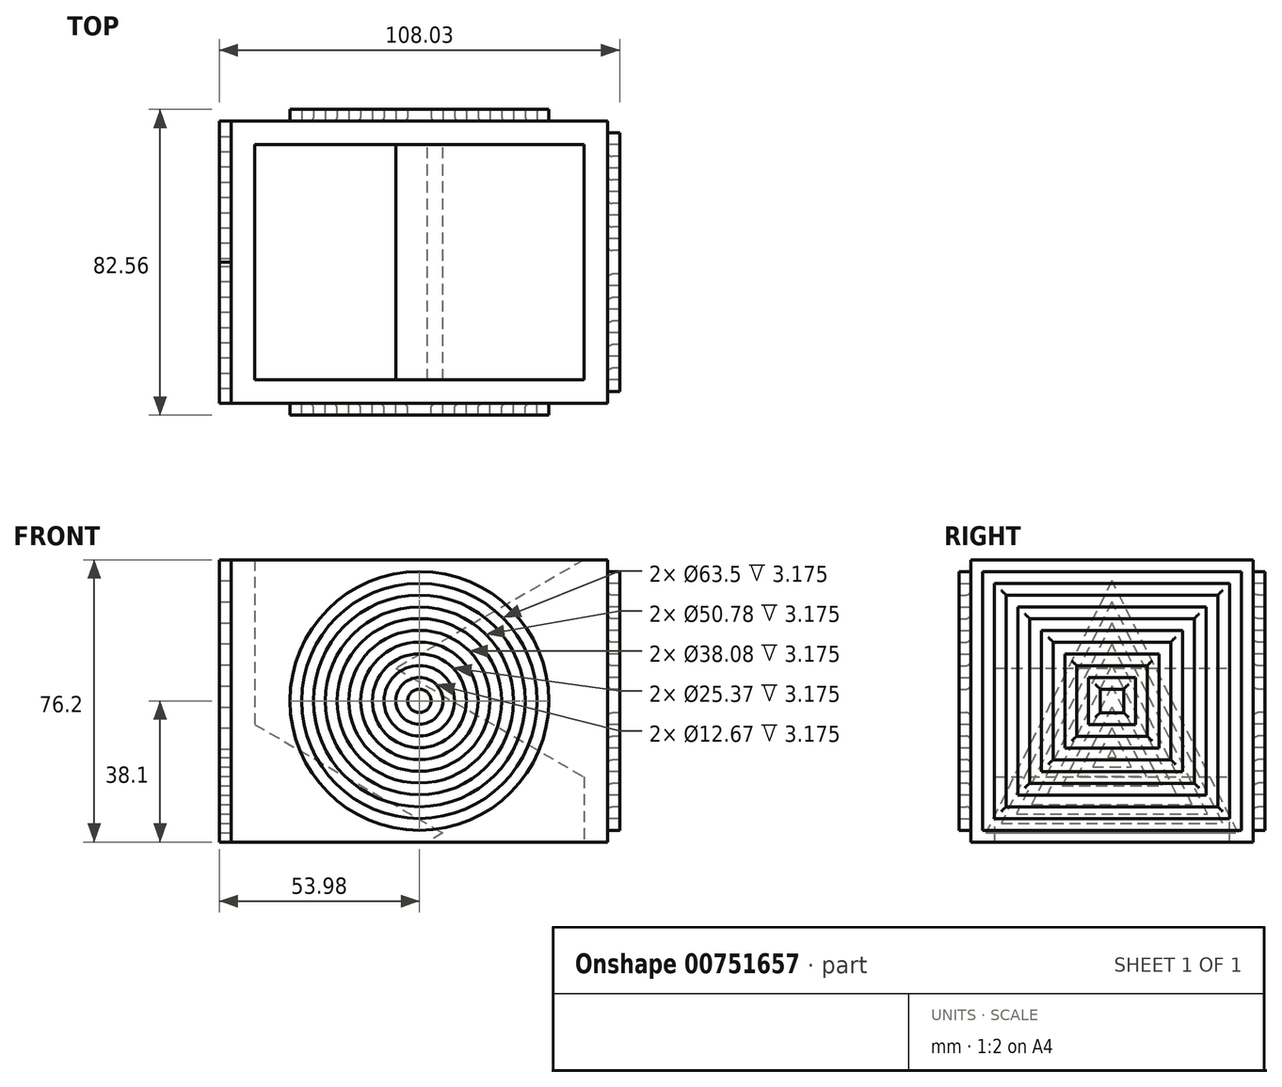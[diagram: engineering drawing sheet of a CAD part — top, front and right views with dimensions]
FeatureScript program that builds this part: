
annotation { "Feature Type Name" : "Feature", "Feature Type Description" : "" }
export const myFeature = defineFeature(function(context is Context, id is Id, definition is map)
    precondition{}
    {
        {
            var Q0;
            Q0=qCreatedBy(makeId("Front.planeOp"),FACE);
            var sketch = newSketch(context, id + "F0", { "sketchPlane" : qUnion([Q0])});
            skLineSegment(sketch, "E0", {"start": v(50.8, 38.1) * mm, "end": v(50.8, -38.1) * mm});
            skLineSegment(sketch, "E1", {"start": v(50.8, 38.1) * mm, "end": v(-50.8, 38.1) * mm});
            skLineSegment(sketch, "E2.MirrorCS", {"start": v(-50.8, 38.1) * mm, "end": v(-50.8, -38.1) * mm});
            skLineSegment(sketch, "E3.MirrorCS", {"start": v(-50.8, 38.1) * mm, "end": v(50.8, 38.1) * mm});
            skLineSegment(sketch, "E4.MirrorCS", {"start": v(-50.8, -38.1) * mm, "end": v(50.8, -38.1) * mm});
            skLineSegment(sketch, "E5", {"start": v(44.45, 38.1) * mm, "end": v(44.45, -38.1) * mm});
            skLineSegment(sketch, "E6", {"start": v(-44.45, 38.1) * mm, "end": v(-44.45, -38.1) * mm});
            skLineSegment(sketch, "E7", {"start": v(44.45, 38.1) * mm, "end": v(-6.35, 8.77) * mm});
            skLineSegment(sketch, "E8", {"start": v(-6.35, 8.77) * mm, "end": v(44.45, -20.56) * mm});
            skLineSegment(sketch, "E9", {"start": v(-44.45, -6.35) * mm, "end": v(6.35, -35.68) * mm});
            skLineSegment(sketch, "E10", {"start": v(6.35, -35.68) * mm, "end": v(2.16, -38.1) * mm});
            skSolve(sketch);
        }
        {
            var Q0;
            {var subQ0=sQuery(id+"F0.wireOp",EDGE,"E7");Q0=makeQuery(id+"F0.imprint","IMPRINT",FACE,{"disambiguationData":[TD([[makeQuery(id+"F0.imprint","IMPRINT",EDGE,{"derivedFrom":subQ0}),1.0]])]});}
            var Q1;
            {var subQ1=sQuery(id+"F0.wireOp",EDGE,"E0");Q1=makeQuery(id+"F0.imprint","IMPRINT",FACE,{"disambiguationData":[TD([[makeQuery(id+"F0.imprint","IMPRINT",EDGE,{"derivedFrom":subQ1}),-1.0]])]});}
            var Q2;
            {var subQ4=sQuery(id+"F0.wireOp",EDGE,"E9");Q2=makeQuery(id+"F0.imprint","IMPRINT",FACE,{"disambiguationData":[TD([[makeQuery(id+"F0.imprint","IMPRINT",EDGE,{"derivedFrom":subQ4}),-1.0]])]});}
            var Q3;
            {var subQ1=sQuery(id+"F0.wireOp",EDGE,"E2.MirrorCS");Q3=makeQuery(id+"F0.imprint","IMPRINT",FACE,{"disambiguationData":[TD([[makeQuery(id+"F0.imprint","IMPRINT",EDGE,{"derivedFrom":subQ1}),1.0]])]});}
            extrude(context, id + "F1", {"entities" : qUnion([Q0, Q1, Q2, Q3]), "endBound" : BoundingType.SYMMETRIC, "depth" : 76.2 * mm, "offsetDistance" : 25.4 * mm});
        }
        {
            var Q0;
            Q0=makeQuery(id+"F1.opExtrude","CAP_FACE",FACE,{"disambiguationData":[OSD([sQuery(id+"F0.wireOp",EDGE,"E0"),sQuery(id+"F0.wireOp",EDGE,"E3.MirrorCS"),sQuery(id+"F0.wireOp",EDGE,"E4.MirrorCS"),sQuery(id+"F0.wireOp",EDGE,"E5"),sQuery(id+"F0.wireOp",EDGE,"E7"),sQuery(id+"F0.wireOp",EDGE,"E8")])],"isStart":true});
            var sketch = newSketch(context, id + "F2", { "sketchPlane" : qUnion([Q0])});
            skLineSegment(sketch, "E11.bottom", {"start": v(50.8, 38.1) * mm, "end": v(-50.8, 38.1) * mm});
            skLineSegment(sketch, "E11.top", {"start": v(50.8, -38.1) * mm, "end": v(-50.8, -38.1) * mm});
            skLineSegment(sketch, "E11.left", {"start": v(50.8, 38.1) * mm, "end": v(50.8, -38.1) * mm});
            skLineSegment(sketch, "E11.right", {"start": v(-50.8, 38.1) * mm, "end": v(-50.8, -38.1) * mm});
            skPoint(sketch, "E11.middle", {"position": v(0, 0) * mm});
            skSolve(sketch);
        }
        {
            var Q0;
            Q0 = qSketchRegion(id + "F2", true);
            extrude(context, id + "F3", {"entities" : qUnion([Q0]), "operationType" : NewBodyOperationType.ADD, "oppositeDirection" : true, "depth" : 6.35 * mm, "offsetDistance" : 25.4 * mm});
        }
        {
            var Q0;
            Q0=makeQuery(id+"F1.opExtrude","CAP_FACE",FACE,{"disambiguationData":[OSD([sQuery(id+"F0.wireOp",EDGE,"E0"),sQuery(id+"F0.wireOp",EDGE,"E3.MirrorCS"),sQuery(id+"F0.wireOp",EDGE,"E4.MirrorCS"),sQuery(id+"F0.wireOp",EDGE,"E5"),sQuery(id+"F0.wireOp",EDGE,"E7"),sQuery(id+"F0.wireOp",EDGE,"E8")])],"isStart":false});
            var sketch = newSketch(context, id + "F4", { "sketchPlane" : qUnion([Q0])});
            skLineSegment(sketch, "E12.bottom", {"start": v(50.8, -38.1) * mm, "end": v(-50.8, -38.1) * mm});
            skLineSegment(sketch, "E12.top", {"start": v(50.8, 38.1) * mm, "end": v(-50.8, 38.1) * mm});
            skLineSegment(sketch, "E12.left", {"start": v(50.8, -38.1) * mm, "end": v(50.8, 38.1) * mm});
            skLineSegment(sketch, "E12.right", {"start": v(-50.8, -38.1) * mm, "end": v(-50.8, 38.1) * mm});
            skPoint(sketch, "E12.middle", {"position": v(0, 0) * mm});
            skSolve(sketch);
        }
        {
            var Q0;
            Q0 = qSketchRegion(id + "F4", true);
            extrude(context, id + "F5", {"entities" : qUnion([Q0]), "operationType" : NewBodyOperationType.ADD, "oppositeDirection" : true, "depth" : 6.35 * mm, "offsetDistance" : 25.4 * mm});
        }
        {
            var Q0;
            Q0=makeQuery(id+"F1.opExtrude","SWEPT_FACE",FACE,{"disambiguationData":[OSD([sQuery(id+"F0.wireOp",EDGE,"E0")])]});
            var sketch = newSketch(context, id + "F6", { "sketchPlane" : qUnion([Q0])});
            skLineSegment(sketch, "E13.bottom", {"start": v(-34.93, 34.92) * mm, "end": v(34.93, 34.92) * mm});
            skLineSegment(sketch, "E13.top", {"start": v(-34.93, -34.92) * mm, "end": v(34.93, -34.92) * mm});
            skLineSegment(sketch, "E13.left", {"start": v(-34.92, 34.92) * mm, "end": v(-34.92, -34.92) * mm});
            skLineSegment(sketch, "E13.right", {"start": v(34.93, 34.92) * mm, "end": v(34.93, -34.92) * mm});
            skPoint(sketch, "E13.middle", {"position": v(0, 0) * mm});
            skLineSegment(sketch, "E14.bottom", {"start": v(-31.75, 31.75) * mm, "end": v(31.75, 31.75) * mm});
            skLineSegment(sketch, "E14.top", {"start": v(-31.75, -31.75) * mm, "end": v(31.75, -31.75) * mm});
            skLineSegment(sketch, "E14.left", {"start": v(-31.75, 31.75) * mm, "end": v(-31.75, -31.75) * mm});
            skLineSegment(sketch, "E14.right", {"start": v(31.75, 31.75) * mm, "end": v(31.75, -31.75) * mm});
            skLineSegment(sketch, "E15.bottom", {"start": v(-28.57, 28.57) * mm, "end": v(28.57, 28.57) * mm});
            skLineSegment(sketch, "E15.top", {"start": v(-28.57, -28.57) * mm, "end": v(28.57, -28.57) * mm});
            skLineSegment(sketch, "E15.left", {"start": v(-28.57, 28.57) * mm, "end": v(-28.57, -28.57) * mm});
            skLineSegment(sketch, "E15.right", {"start": v(28.58, 28.57) * mm, "end": v(28.58, -28.57) * mm});
            skLineSegment(sketch, "E16.bottom", {"start": v(-25.4, 25.4) * mm, "end": v(25.4, 25.4) * mm});
            skLineSegment(sketch, "E16.top", {"start": v(-25.4, -25.4) * mm, "end": v(25.4, -25.4) * mm});
            skLineSegment(sketch, "E16.left", {"start": v(-25.4, 25.4) * mm, "end": v(-25.4, -25.4) * mm});
            skLineSegment(sketch, "E16.right", {"start": v(25.4, 25.4) * mm, "end": v(25.4, -25.4) * mm});
            skLineSegment(sketch, "E17.bottom", {"start": v(-22.23, 22.23) * mm, "end": v(22.23, 22.23) * mm});
            skLineSegment(sketch, "E17.top", {"start": v(-22.23, -22.23) * mm, "end": v(22.23, -22.23) * mm});
            skLineSegment(sketch, "E17.left", {"start": v(-22.23, 22.23) * mm, "end": v(-22.23, -22.23) * mm});
            skLineSegment(sketch, "E17.right", {"start": v(22.23, 22.23) * mm, "end": v(22.23, -22.23) * mm});
            skLineSegment(sketch, "E18.bottom", {"start": v(-19.05, 19.05) * mm, "end": v(19.05, 19.05) * mm});
            skLineSegment(sketch, "E18.top", {"start": v(-19.05, -19.05) * mm, "end": v(19.05, -19.05) * mm});
            skLineSegment(sketch, "E18.left", {"start": v(-19.05, 19.05) * mm, "end": v(-19.05, -19.05) * mm});
            skLineSegment(sketch, "E18.right", {"start": v(19.05, 19.05) * mm, "end": v(19.05, -19.05) * mm});
            skLineSegment(sketch, "E19.bottom", {"start": v(-15.88, 15.88) * mm, "end": v(15.88, 15.88) * mm});
            skLineSegment(sketch, "E19.top", {"start": v(-15.88, -15.88) * mm, "end": v(15.88, -15.88) * mm});
            skLineSegment(sketch, "E19.left", {"start": v(-15.88, 15.88) * mm, "end": v(-15.88, -15.88) * mm});
            skLineSegment(sketch, "E19.right", {"start": v(15.88, 15.88) * mm, "end": v(15.88, -15.88) * mm});
            skLineSegment(sketch, "E20.bottom", {"start": v(-12.7, 12.7) * mm, "end": v(12.7, 12.7) * mm});
            skLineSegment(sketch, "E20.top", {"start": v(-12.7, -12.7) * mm, "end": v(12.7, -12.7) * mm});
            skLineSegment(sketch, "E20.left", {"start": v(-12.7, 12.7) * mm, "end": v(-12.7, -12.7) * mm});
            skLineSegment(sketch, "E20.right", {"start": v(12.7, 12.7) * mm, "end": v(12.7, -12.7) * mm});
            skLineSegment(sketch, "E21.bottom", {"start": v(-9.52, 9.52) * mm, "end": v(9.52, 9.52) * mm});
            skLineSegment(sketch, "E21.top", {"start": v(-9.52, -9.52) * mm, "end": v(9.52, -9.52) * mm});
            skLineSegment(sketch, "E21.left", {"start": v(-9.52, 9.52) * mm, "end": v(-9.52, -9.52) * mm});
            skLineSegment(sketch, "E21.right", {"start": v(9.52, 9.52) * mm, "end": v(9.52, -9.52) * mm});
            skLineSegment(sketch, "E22.bottom", {"start": v(-6.35, 6.35) * mm, "end": v(6.35, 6.35) * mm});
            skLineSegment(sketch, "E22.top", {"start": v(-6.35, -6.35) * mm, "end": v(6.35, -6.35) * mm});
            skLineSegment(sketch, "E22.left", {"start": v(-6.35, 6.35) * mm, "end": v(-6.35, -6.35) * mm});
            skLineSegment(sketch, "E22.right", {"start": v(6.35, 6.35) * mm, "end": v(6.35, -6.35) * mm});
            skLineSegment(sketch, "E23.bottom", {"start": v(-3.17, 3.17) * mm, "end": v(3.17, 3.17) * mm});
            skLineSegment(sketch, "E23.top", {"start": v(-3.17, -3.17) * mm, "end": v(3.17, -3.17) * mm});
            skLineSegment(sketch, "E23.left", {"start": v(-3.17, 3.17) * mm, "end": v(-3.17, -3.17) * mm});
            skLineSegment(sketch, "E23.right", {"start": v(3.17, 3.17) * mm, "end": v(3.17, -3.17) * mm});
            skSolve(sketch);
        }
        {
            var Q0;
            Q0 = qSketchRegion(id + "F6", true);
            var Q1;
            Q1=makeQuery(id+"F6.imprint","IMPRINT",FACE,{"disambiguationData":[TD([[makeQuery(id+"F6.imprint","IMPRINT",EDGE,{"derivedFrom":sQuery(id+"F6.wireOp",EDGE,"E15.bottom")}),-1.0]])]});
            var Q2;
            Q2=makeQuery(id+"F6.imprint","IMPRINT",FACE,{"disambiguationData":[TD([[makeQuery(id+"F6.imprint","IMPRINT",EDGE,{"derivedFrom":sQuery(id+"F6.wireOp",EDGE,"E17.bottom")}),-1.0]])]});
            var Q3;
            Q3=makeQuery(id+"F6.imprint","IMPRINT",FACE,{"disambiguationData":[TD([[makeQuery(id+"F6.imprint","IMPRINT",EDGE,{"derivedFrom":sQuery(id+"F6.wireOp",EDGE,"E19.bottom")}),-1.0]])]});
            var Q4;
            Q4=makeQuery(id+"F6.imprint","IMPRINT",FACE,{"disambiguationData":[TD([[makeQuery(id+"F6.imprint","IMPRINT",EDGE,{"derivedFrom":sQuery(id+"F6.wireOp",EDGE,"E21.bottom")}),-1.0]])]});
            var Q5;
            Q5=makeQuery(id+"F6.imprint","IMPRINT",FACE,{"disambiguationData":[TD([[makeQuery(id+"F6.imprint","IMPRINT",EDGE,{"derivedFrom":sQuery(id+"F6.wireOp",EDGE,"E23.bottom")}),-1.0]])]});
            extrude(context, id + "F7", {"entities" : qUnion([Q0, Q1, Q2, Q3, Q4, Q5]), "operationType" : NewBodyOperationType.ADD, "depth" : 3.25 * mm, "offsetDistance" : 25.4 * mm});
        }
        {
            var Q0;
            {var subQ0=sQuery(id+"F0.wireOp",EDGE,"E4.MirrorCS");var subQ1=sQuery(id+"F0.wireOp",EDGE,"E3.MirrorCS");Q0=makeQuery(id+"F3.boolean.opBoolean","MERGE",FACE,{"derivedFrom":[makeQuery(id+"F1.opExtrude","CAP_FACE",FACE,{"disambiguationData":[OSD([sQuery(id+"F0.wireOp",EDGE,"E0"),subQ1,subQ0,sQuery(id+"F0.wireOp",EDGE,"E5"),sQuery(id+"F0.wireOp",EDGE,"E7"),sQuery(id+"F0.wireOp",EDGE,"E8")])],"isStart":true}),makeQuery(id+"F1.opExtrude","CAP_FACE",FACE,{"disambiguationData":[OSD([sQuery(id+"F0.wireOp",EDGE,"E2.MirrorCS"),subQ1,subQ0,sQuery(id+"F0.wireOp",EDGE,"E6"),sQuery(id+"F0.wireOp",EDGE,"E9"),sQuery(id+"F0.wireOp",EDGE,"E10")])],"isStart":true}),makeQuery(id+"F3.opExtrude","CAP_FACE",FACE,{"disambiguationData":[OSD([sQuery(id+"F2.wireOp",EDGE,"E11.bottom"),sQuery(id+"F2.wireOp",EDGE,"E11.top"),sQuery(id+"F2.wireOp",EDGE,"E11.left"),sQuery(id+"F2.wireOp",EDGE,"E11.right")])],"isStart":true})]});}
            var sketch = newSketch(context, id + "F8", { "sketchPlane" : qUnion([Q0])});
            skCircle(sketch, "E24", {"center": v(0, 0) * mm, "radius": 34.93 * mm});
            skCircle(sketch, "E25", {"center": v(0, 0) * mm, "radius": 31.75 * mm});
            skCircle(sketch, "E26", {"center": v(0, 0) * mm, "radius": 28.58 * mm});
            skCircle(sketch, "E27", {"center": v(0, 0) * mm, "radius": 25.4 * mm});
            skCircle(sketch, "E28", {"center": v(0, 0) * mm, "radius": 22.22 * mm});
            skCircle(sketch, "E29", {"center": v(0, 0) * mm, "radius": 19.04 * mm});
            skCircle(sketch, "E30", {"center": v(0, 0) * mm, "radius": 15.86 * mm});
            skCircle(sketch, "E31", {"center": v(0, 0) * mm, "radius": 12.68 * mm});
            skCircle(sketch, "E32", {"center": v(0, 0) * mm, "radius": 9.5 * mm});
            skCircle(sketch, "E33", {"center": v(0, 0) * mm, "radius": 6.33 * mm});
            skCircle(sketch, "E34", {"center": v(0, 0) * mm, "radius": 3.16 * mm});
            skSolve(sketch);
        }
        {
            var Q0;
            Q0 = qSketchRegion(id + "F8", true);
            var Q1;
            Q1=makeQuery(id+"F8.imprint","IMPRINT",FACE,{"disambiguationData":[TD([[makeQuery(id+"F8.imprint","IMPRINT",EDGE,{"derivedFrom":sQuery(id+"F8.wireOp",EDGE,"E26")}),1.0]])]});
            var Q2;
            Q2=makeQuery(id+"F8.imprint","IMPRINT",FACE,{"disambiguationData":[TD([[makeQuery(id+"F8.imprint","IMPRINT",EDGE,{"derivedFrom":sQuery(id+"F8.wireOp",EDGE,"E28")}),1.0]])]});
            var Q3;
            Q3=makeQuery(id+"F8.imprint","IMPRINT",FACE,{"disambiguationData":[TD([[makeQuery(id+"F8.imprint","IMPRINT",EDGE,{"derivedFrom":sQuery(id+"F8.wireOp",EDGE,"E30")}),1.0]])]});
            var Q4;
            Q4=makeQuery(id+"F8.imprint","IMPRINT",FACE,{"disambiguationData":[TD([[makeQuery(id+"F8.imprint","IMPRINT",EDGE,{"derivedFrom":sQuery(id+"F8.wireOp",EDGE,"E32")}),1.0]])]});
            var Q5;
            Q5=makeQuery(id+"F8.imprint","IMPRINT",FACE,{"disambiguationData":[TD([[makeQuery(id+"F8.imprint","IMPRINT",EDGE,{"derivedFrom":sQuery(id+"F8.wireOp",EDGE,"E34")}),1.0]])]});
            extrude(context, id + "F9", {"entities" : qUnion([Q0, Q1, Q2, Q3, Q4, Q5]), "operationType" : NewBodyOperationType.ADD, "depth" : 3.17 * mm, "offsetDistance" : 25.4 * mm});
        }
        {
            var Q0;
            Q0=makeQuery(id+"F7.opExtrude","CAP_EDGE",EDGE,{"disambiguationData":[OSD([sQuery(id+"F6.wireOp",EDGE,"E13.left")])],"isStart":true});
            var Q1;
            Q1=makeQuery(id+"F7.opExtrude","CAP_EDGE",EDGE,{"disambiguationData":[OSD([sQuery(id+"F6.wireOp",EDGE,"E13.bottom")])],"isStart":true});
            var Q2;
            Q2=makeQuery(id+"F7.opExtrude","CAP_EDGE",EDGE,{"disambiguationData":[OSD([sQuery(id+"F6.wireOp",EDGE,"E13.right")])],"isStart":true});
            var Q3;
            Q3=makeQuery(id+"F7.opExtrude","CAP_EDGE",EDGE,{"disambiguationData":[OSD([sQuery(id+"F6.wireOp",EDGE,"E13.top")])],"isStart":true});
            var Q4;
            Q4=makeQuery(id+"F7.opExtrude","CAP_EDGE",EDGE,{"disambiguationData":[OSD([sQuery(id+"F6.wireOp",EDGE,"E15.right")])],"isStart":true});
            var Q5;
            Q5=makeQuery(id+"F7.opExtrude","CAP_EDGE",EDGE,{"disambiguationData":[OSD([sQuery(id+"F6.wireOp",EDGE,"E15.bottom")])],"isStart":true});
            var Q6;
            Q6=makeQuery(id+"F7.opExtrude","CAP_EDGE",EDGE,{"disambiguationData":[OSD([sQuery(id+"F6.wireOp",EDGE,"E15.left")])],"isStart":true});
            var Q7;
            Q7=makeQuery(id+"F7.opExtrude","CAP_EDGE",EDGE,{"disambiguationData":[OSD([sQuery(id+"F6.wireOp",EDGE,"E15.top")])],"isStart":true});
            var Q8;
            Q8=makeQuery(id+"F7.opExtrude","CAP_EDGE",EDGE,{"disambiguationData":[OSD([sQuery(id+"F6.wireOp",EDGE,"E17.top")])],"isStart":true});
            var Q9;
            Q9=makeQuery(id+"F7.opExtrude","CAP_EDGE",EDGE,{"disambiguationData":[OSD([sQuery(id+"F6.wireOp",EDGE,"E17.left")])],"isStart":true});
            var Q10;
            Q10=makeQuery(id+"F7.opExtrude","CAP_EDGE",EDGE,{"disambiguationData":[OSD([sQuery(id+"F6.wireOp",EDGE,"E17.right")])],"isStart":true});
            var Q11;
            Q11=makeQuery(id+"F7.opExtrude","CAP_EDGE",EDGE,{"disambiguationData":[OSD([sQuery(id+"F6.wireOp",EDGE,"E17.bottom")])],"isStart":true});
            var Q12;
            Q12=makeQuery(id+"F7.opExtrude","CAP_EDGE",EDGE,{"disambiguationData":[OSD([sQuery(id+"F6.wireOp",EDGE,"E19.bottom")])],"isStart":true});
            var Q13;
            Q13=makeQuery(id+"F7.opExtrude","CAP_EDGE",EDGE,{"disambiguationData":[OSD([sQuery(id+"F6.wireOp",EDGE,"E19.right")])],"isStart":true});
            var Q14;
            Q14=makeQuery(id+"F7.opExtrude","CAP_EDGE",EDGE,{"disambiguationData":[OSD([sQuery(id+"F6.wireOp",EDGE,"E21.bottom")])],"isStart":true});
            var Q15;
            Q15=makeQuery(id+"F7.opExtrude","CAP_EDGE",EDGE,{"disambiguationData":[OSD([sQuery(id+"F6.wireOp",EDGE,"E21.right")])],"isStart":true});
            var Q16;
            Q16=makeQuery(id+"F7.opExtrude","CAP_EDGE",EDGE,{"disambiguationData":[OSD([sQuery(id+"F6.wireOp",EDGE,"E23.bottom")])],"isStart":true});
            var Q17;
            Q17=makeQuery(id+"F7.opExtrude","CAP_EDGE",EDGE,{"disambiguationData":[OSD([sQuery(id+"F6.wireOp",EDGE,"E23.right")])],"isStart":true});
            var Q18;
            Q18=makeQuery(id+"F7.opExtrude","CAP_EDGE",EDGE,{"disambiguationData":[OSD([sQuery(id+"F6.wireOp",EDGE,"E23.left")])],"isStart":true});
            var Q19;
            Q19=makeQuery(id+"F7.opExtrude","CAP_EDGE",EDGE,{"disambiguationData":[OSD([sQuery(id+"F6.wireOp",EDGE,"E23.top")])],"isStart":true});
            var Q20;
            Q20=makeQuery(id+"F7.opExtrude","CAP_EDGE",EDGE,{"disambiguationData":[OSD([sQuery(id+"F6.wireOp",EDGE,"E21.left")])],"isStart":true});
            var Q21;
            Q21=makeQuery(id+"F7.opExtrude","CAP_EDGE",EDGE,{"disambiguationData":[OSD([sQuery(id+"F6.wireOp",EDGE,"E21.top")])],"isStart":true});
            var Q22;
            Q22=makeQuery(id+"F7.opExtrude","CAP_EDGE",EDGE,{"disambiguationData":[OSD([sQuery(id+"F6.wireOp",EDGE,"E19.left")])],"isStart":true});
            var Q23;
            Q23=makeQuery(id+"F7.opExtrude","CAP_EDGE",EDGE,{"disambiguationData":[OSD([sQuery(id+"F6.wireOp",EDGE,"E19.top")])],"isStart":true});
            fillet(context, id + "F10", {"entities" : qUnion([Q0, Q1, Q2, Q3, Q4, Q5, Q6, Q7, Q8, Q9, Q10, Q11, Q12, Q13, Q14, Q15, Q16, Q17, Q18, Q19, Q20, Q21, Q22, Q23]), "radius" : 1.27 * mm, "tangentPropagation" : true, "allowEdgeOverflow" : false});
        }
        {
            var Q0;
            Q0=makeQuery(id+"F9.opExtrude","CAP_EDGE",EDGE,{"disambiguationData":[OSD([sQuery(id+"F8.wireOp",EDGE,"E24")])],"isStart":true});
            var Q1;
            Q1=makeQuery(id+"F9.opExtrude","CAP_EDGE",EDGE,{"disambiguationData":[OSD([sQuery(id+"F8.wireOp",EDGE,"E26")])],"isStart":true});
            var Q2;
            Q2=makeQuery(id+"F9.opExtrude","CAP_EDGE",EDGE,{"disambiguationData":[OSD([sQuery(id+"F8.wireOp",EDGE,"E28")])],"isStart":true});
            var Q3;
            Q3=makeQuery(id+"F9.opExtrude","CAP_EDGE",EDGE,{"disambiguationData":[OSD([sQuery(id+"F8.wireOp",EDGE,"E30")])],"isStart":true});
            var Q4;
            Q4=makeQuery(id+"F9.opExtrude","CAP_EDGE",EDGE,{"disambiguationData":[OSD([sQuery(id+"F8.wireOp",EDGE,"E32")])],"isStart":true});
            var Q5;
            Q5=makeQuery(id+"F9.opExtrude","CAP_EDGE",EDGE,{"disambiguationData":[OSD([sQuery(id+"F8.wireOp",EDGE,"E34")])],"isStart":true});
            fillet(context, id + "F11", {"entities" : qUnion([Q0, Q1, Q2, Q3, Q4, Q5]), "radius" : 1.27 * mm, "tangentPropagation" : true, "allowEdgeOverflow" : false});
        }
        {
            var Q0;
            Q0=makeQuery(id+"F1.opExtrude","SWEPT_BODY",BODY,{"disambiguationData":[OSD([sQuery(id+"F0.wireOp",EDGE,"E0"),sQuery(id+"F0.wireOp",EDGE,"E3.MirrorCS"),sQuery(id+"F0.wireOp",EDGE,"E4.MirrorCS"),sQuery(id+"F0.wireOp",EDGE,"E5"),sQuery(id+"F0.wireOp",EDGE,"E7"),sQuery(id+"F0.wireOp",EDGE,"E8")])]});
            var Q1;
            Q1=qCreatedBy(makeId("Front.planeOp"),FACE);
            mirror(context, id + "F12", {"operationType" : NewBodyOperationType.ADD, "entities" : qUnion([Q0]), "mirrorPlane" : qUnion([Q1])});
        }
        {
            var Q0;
            Q0=makeQuery(id+"F1.opExtrude","SWEPT_FACE",FACE,{"disambiguationData":[OSD([sQuery(id+"F0.wireOp",EDGE,"E2.MirrorCS")])]});
            var sketch = newSketch(context, id + "F13", { "sketchPlane" : qUnion([Q0])});
            skLineSegment(sketch, "E35.0", {"start": v(38.1, -38.1) * mm, "end": v(-38.1, -38.1) * mm});
            skLineSegment(sketch, "E36", {"start": v(-38.1, -38.1) * mm, "end": v(0, 38.1) * mm});
            skLineSegment(sketch, "E37", {"start": v(0, 38.1) * mm, "end": v(38.1, -38.1) * mm});
            skLineSegment(sketch, "E38.0", {"start": v(-34, -35.56) * mm, "end": v(0, 32.42) * mm});
            skLineSegment(sketch, "E38.1", {"start": v(34, -35.56) * mm, "end": v(-34, -35.56) * mm});
            skLineSegment(sketch, "E38.2", {"start": v(0, 32.42) * mm, "end": v(34, -35.56) * mm});
            skLineSegment(sketch, "E39.0", {"start": v(-29.88, -33.02) * mm, "end": v(0, 26.74) * mm});
            skLineSegment(sketch, "E39.1", {"start": v(29.88, -33.02) * mm, "end": v(-29.88, -33.02) * mm});
            skLineSegment(sketch, "E39.2", {"start": v(0, 26.74) * mm, "end": v(29.88, -33.02) * mm});
            skLineSegment(sketch, "E40.0", {"start": v(-25.77, -30.48) * mm, "end": v(0, 21.06) * mm});
            skLineSegment(sketch, "E40.1", {"start": v(25.77, -30.48) * mm, "end": v(-25.77, -30.48) * mm});
            skLineSegment(sketch, "E40.2", {"start": v(0, 21.06) * mm, "end": v(25.77, -30.48) * mm});
            skLineSegment(sketch, "E41.0", {"start": v(-21.66, -27.94) * mm, "end": v(0, 15.38) * mm});
            skLineSegment(sketch, "E41.1", {"start": v(21.66, -27.94) * mm, "end": v(-21.66, -27.94) * mm});
            skLineSegment(sketch, "E41.2", {"start": v(0, 15.38) * mm, "end": v(21.66, -27.94) * mm});
            skLineSegment(sketch, "E42.0", {"start": v(-17.55, -25.4) * mm, "end": v(0, 9.7) * mm});
            skLineSegment(sketch, "E42.1", {"start": v(17.55, -25.4) * mm, "end": v(-17.55, -25.4) * mm});
            skLineSegment(sketch, "E42.2", {"start": v(0, 9.7) * mm, "end": v(17.55, -25.4) * mm});
            skLineSegment(sketch, "E43.0", {"start": v(-13.44, -22.86) * mm, "end": v(0, 4.02) * mm});
            skLineSegment(sketch, "E43.1", {"start": v(13.44, -22.86) * mm, "end": v(-13.44, -22.86) * mm});
            skLineSegment(sketch, "E43.2", {"start": v(0, 4.02) * mm, "end": v(13.44, -22.86) * mm});
            skLineSegment(sketch, "E44.0", {"start": v(-9.33, -20.32) * mm, "end": v(0, -1.66) * mm});
            skLineSegment(sketch, "E44.1", {"start": v(9.33, -20.32) * mm, "end": v(-9.33, -20.32) * mm});
            skLineSegment(sketch, "E44.2", {"start": v(0, -1.66) * mm, "end": v(9.33, -20.32) * mm});
            skLineSegment(sketch, "E45.0", {"start": v(0, -7.34) * mm, "end": v(5.22, -17.78) * mm});
            skLineSegment(sketch, "E45.1", {"start": v(-5.22, -17.78) * mm, "end": v(0, -7.34) * mm});
            skLineSegment(sketch, "E46.0", {"start": v(5.22, -17.78) * mm, "end": v(-5.22, -17.78) * mm});
            skLineSegment(sketch, "E47.0", {"start": v(-1.11, -15.24) * mm, "end": v(0, -13.02) * mm});
            skLineSegment(sketch, "E48.0", {"start": v(0, -13.02) * mm, "end": v(1.11, -15.24) * mm});
            skLineSegment(sketch, "E49.0", {"start": v(1.11, -15.24) * mm, "end": v(-1.11, -15.24) * mm});
            skSolve(sketch);
        }
        {
            var Q0;
            Q0 = qSketchRegion(id + "F13", true);
            var Q1;
            Q1=makeQuery(id+"F13.imprint","IMPRINT",FACE,{"disambiguationData":[TD([[makeQuery(id+"F13.imprint","IMPRINT",EDGE,{"derivedFrom":sQuery(id+"F13.wireOp",EDGE,"E39.0")}),-1.0]])]});
            var Q2;
            Q2=makeQuery(id+"F13.imprint","IMPRINT",FACE,{"disambiguationData":[TD([[makeQuery(id+"F13.imprint","IMPRINT",EDGE,{"derivedFrom":sQuery(id+"F13.wireOp",EDGE,"E41.0")}),-1.0]])]});
            var Q3;
            Q3=makeQuery(id+"F13.imprint","IMPRINT",FACE,{"disambiguationData":[TD([[makeQuery(id+"F13.imprint","IMPRINT",EDGE,{"derivedFrom":sQuery(id+"F13.wireOp",EDGE,"E43.0")}),-1.0]])]});
            var Q4;
            Q4=makeQuery(id+"F13.imprint","IMPRINT",FACE,{"disambiguationData":[TD([[makeQuery(id+"F13.imprint","IMPRINT",EDGE,{"derivedFrom":sQuery(id+"F13.wireOp",EDGE,"E45.0")}),-1.0]])]});
            extrude(context, id + "F14", {"entities" : qUnion([Q0, Q1, Q2, Q3, Q4]), "operationType" : NewBodyOperationType.ADD, "depth" : 3.17 * mm, "offsetDistance" : 25.4 * mm});
        }
    });
